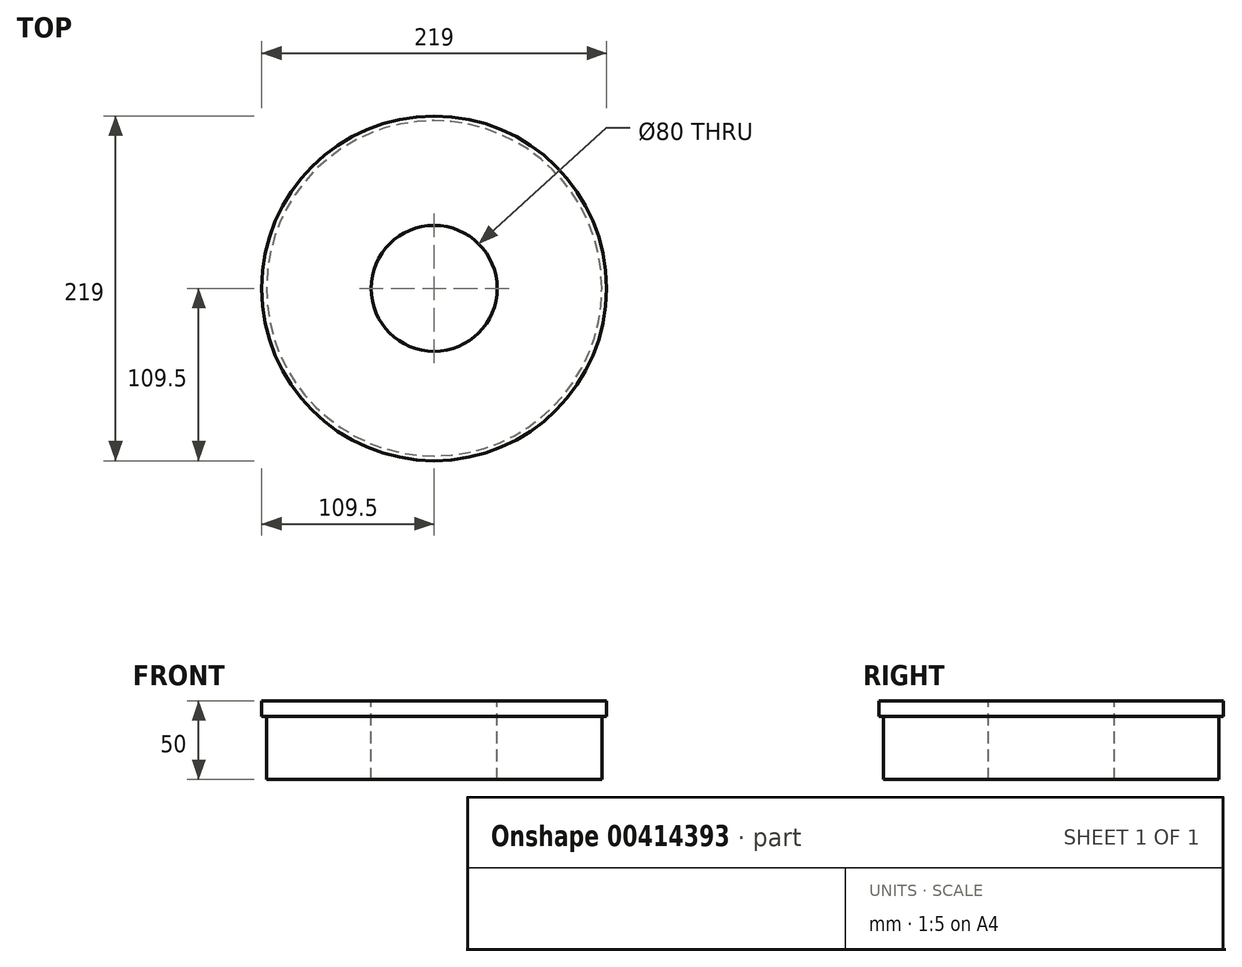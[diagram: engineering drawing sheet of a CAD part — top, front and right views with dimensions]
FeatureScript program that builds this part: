
annotation { "Feature Type Name" : "Feature", "Feature Type Description" : "" }
export const myFeature = defineFeature(function(context is Context, id is Id, definition is map)
    precondition{}
    {
        {
            var Q0;
            Q0=qCreatedBy(makeId("Top.planeOp"),FACE);
            var sketch = newSketch(context, id + "F0", { "sketchPlane" : qUnion([Q0])});
            skCircle(sketch, "E0", {"center": v(0, 0) * mm, "radius": 109.5 * mm});
            skSolve(sketch);
        }
        {
            var Q0;
            Q0 = qSketchRegion(id + "F0", true);
            extrude(context, id + "F1", {"entities" : qUnion([Q0]), "depth" : 50 * mm});
        }
        {
            var Q0;
            Q0=makeQuery(id+"F1.opExtrude","CAP_FACE",FACE,{"disambiguationData":[OSD([sQuery(id+"F0.wireOp",EDGE,"E0")])],"isStart":true});
            var sketch = newSketch(context, id + "F2", { "sketchPlane" : qUnion([Q0])});
            skCircle(sketch, "E1.0", {"center": v(0, 0) * mm, "radius": 106.5 * mm});
            skCircle(sketch, "E2", {"center": v(0, 0) * mm, "radius": 109.5 * mm});
            skSolve(sketch);
        }
        {
            var Q0;
            Q0 = qSketchRegion(id + "F2", true);
            extrude(context, id + "F3", {"entities" : qUnion([Q0]), "operationType" : NewBodyOperationType.REMOVE, "oppositeDirection" : true, "depth" : 40 * mm});
        }
        {
            var Q0;
            Q0=makeQuery(id+"F1.opExtrude","CAP_FACE",FACE,{"disambiguationData":[OSD([sQuery(id+"F0.wireOp",EDGE,"E0")])],"isStart":false});
            var sketch = newSketch(context, id + "F4", { "sketchPlane" : qUnion([Q0])});
            skCircle(sketch, "E3", {"center": v(0, 0) * mm, "radius": 40 * mm});
            skSolve(sketch);
        }
        {
            var Q0;
            Q0 = qSketchRegion(id + "F4", true);
            extrude(context, id + "F5", {"entities" : qUnion([Q0]), "operationType" : NewBodyOperationType.REMOVE, "endBound" : BoundingType.THROUGH_ALL, "oppositeDirection" : true, "depth" : 25 * mm});
        }
    });
